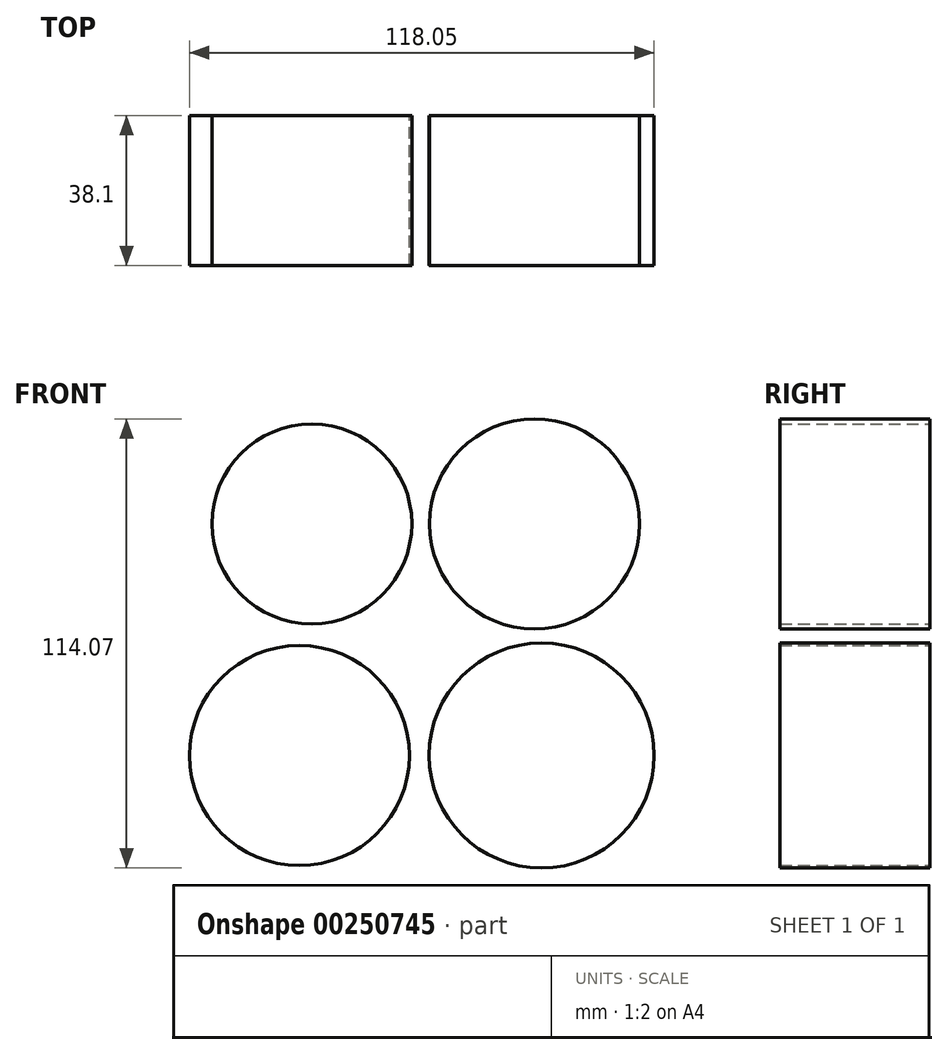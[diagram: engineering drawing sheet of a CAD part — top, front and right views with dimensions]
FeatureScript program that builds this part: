
annotation { "Feature Type Name" : "Feature", "Feature Type Description" : "" }
export const myFeature = defineFeature(function(context is Context, id is Id, definition is map)
    precondition{}
    {
        {
            var Q0;
            Q0=qCreatedBy(makeId("Front.planeOp"),FACE);
            var sketch = newSketch(context, id + "F0", { "sketchPlane" : qUnion([Q0])});
            skCircle(sketch, "E0", {"center": v(-68.8, 48.23) * mm, "radius": 25.4 * mm});
            skCircle(sketch, "E1", {"center": v(-12.23, 48.23) * mm, "radius": 26.67 * mm});
            skCircle(sketch, "E2", {"center": v(-71.96, -10.6) * mm, "radius": 27.94 * mm});
            skCircle(sketch, "E3", {"center": v(-10.43, -10.6) * mm, "radius": 28.58 * mm});
            skSolve(sketch);
        }
        {
            var Q0;
            Q0 = qSketchRegion(id + "F0", true);
            extrude(context, id + "F1", {"entities" : qUnion([Q0]), "depth" : 38.1 * mm});
        }
    });
